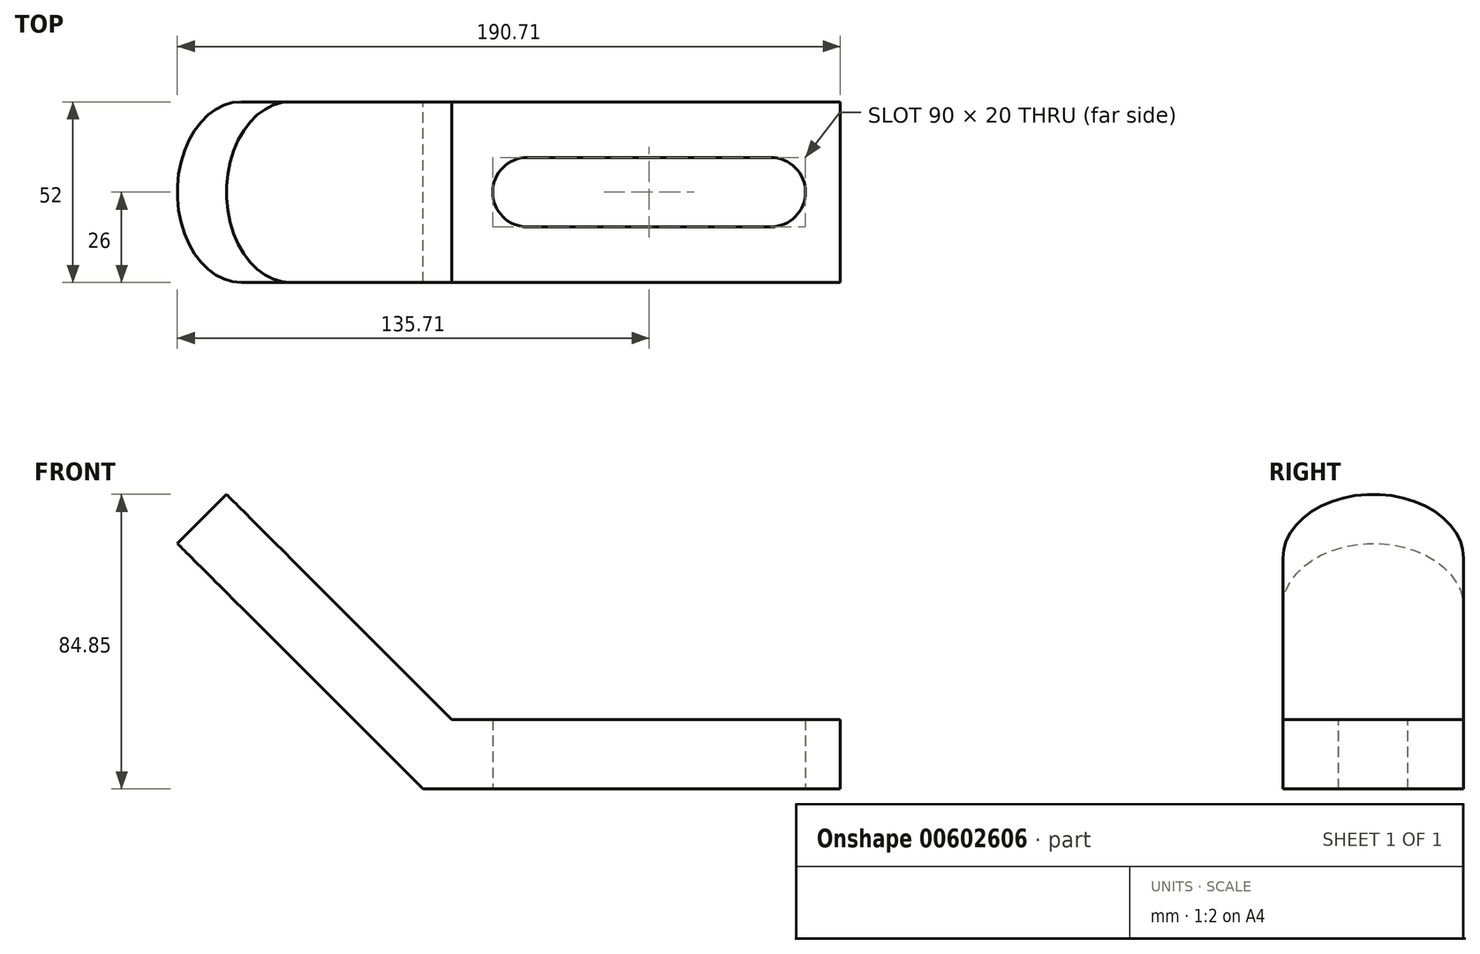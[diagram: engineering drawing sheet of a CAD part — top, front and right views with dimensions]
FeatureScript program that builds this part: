
annotation { "Feature Type Name" : "Feature", "Feature Type Description" : "" }
export const myFeature = defineFeature(function(context is Context, id is Id, definition is map)
    precondition{}
    {
        {
            var Q0;
            Q0=qCreatedBy(makeId("Front.planeOp"),FACE);
            var sketch = newSketch(context, id + "F0", { "sketchPlane" : qUnion([Q0])});
            skLineSegment(sketch, "E0.bottom", {"start": v(0, 0) * mm, "end": v(-120, 0) * mm});
            skLineSegment(sketch, "E0.left", {"start": v(0, 0) * mm, "end": v(0, 20) * mm});
            skLineSegment(sketch, "E1", {"start": v(-120, 0) * mm, "end": v(-190.71, 70.71) * mm});
            skLineSegment(sketch, "E2", {"start": v(-190.71, 70.71) * mm, "end": v(-176.57, 84.85) * mm});
            skLineSegment(sketch, "E3", {"start": v(-176.57, 84.85) * mm, "end": v(-111.72, 20) * mm});
            skLineSegment(sketch, "E4", {"start": v(0, 20) * mm, "end": v(-111.72, 20) * mm});
            skSolve(sketch);
        }
        {
            var Q0;
            Q0=makeQuery(id+"F0.imprint","IMPRINT",FACE,{"disambiguationData":[TD([[makeQuery(id+"F0.imprint","IMPRINT",EDGE,{"derivedFrom":sQuery(id+"F0.wireOp",EDGE,"E0.bottom")}),-1.0]])]});
            var Q1;
            Q1=makeQuery(id+"F0.imprint","IMPRINT",FACE,{"disambiguationData":[TD([[makeQuery(id+"F0.imprint","IMPRINT",EDGE,{"derivedFrom":sQuery(id+"F0.wireOp",EDGE,"n1ADsmMW-Lfod-etTo-9KBK-WFseRF6eV8BT")}),1.0]])]});
            extrude(context, id + "F1", {"entities" : qUnion([Q0, Q1]), "depth" : 52 * mm, "offsetDistance" : 25 * mm});
        }
        {
            var Q0;
            Q0=makeQuery(id+"F1.opExtrude","SWEPT_FACE",FACE,{"disambiguationData":[OSD([sQuery(id+"F0.wireOp",EDGE,"E3")])]});
            var sketch = newSketch(context, id + "F2", { "sketchPlane" : qUnion([Q0])});
            skCircle(sketch, "E5", {"center": v(-158.85, -26) * mm, "radius": 10 * mm});
            skSolve(sketch);
        }
        {
            var Q0;
            Q0=makeQuery(id+"F2.imprint","IMPRINT",FACE,{"disambiguationData":[TD([[makeQuery(id+"F2.imprint","IMPRINT",EDGE,{"derivedFrom":sQuery(id+"F2.wireOp",EDGE,"E5")}),1.0]])]});
            extrude(context, id + "F3", {"entities" : qUnion([Q0]), "operationType" : NewBodyOperationType.REMOVE, "oppositeDirection" : true, "depth" : 25 * mm, "offsetDistance" : 25 * mm});
        }
        {
            var Q0;
            Q0=makeQuery(id+"F1.opExtrude","CAP_EDGE",EDGE,{"disambiguationData":[OSD([sQuery(id+"F0.wireOp",EDGE,"E2")])],"isStart":true});
            var Q1;
            Q1=makeQuery(id+"F1.opExtrude","CAP_EDGE",EDGE,{"disambiguationData":[OSD([sQuery(id+"F0.wireOp",EDGE,"E2")])],"isStart":false});
            fillet(context, id + "F4", {"entities" : qUnion([Q0, Q1]), "radius" : 26 * mm, "tangentPropagation" : true, "allowEdgeOverflow" : false});
        }
        {
            var Q0;
            Q0=makeQuery(id+"F1.opExtrude","SWEPT_FACE",FACE,{"disambiguationData":[OSD([sQuery(id+"F0.wireOp",EDGE,"E4")])]});
            var sketch = newSketch(context, id + "F5", { "sketchPlane" : qUnion([Q0])});
            skLineSegment(sketch, "E6", {"start": v(0, 0) * mm, "end": v(0, -52) * mm});
            skLineSegment(sketch, "E7.top", {"start": v(-100, -16) * mm, "end": v(-10, -16) * mm});
            skLineSegment(sketch, "E7.left", {"start": v(-100, -26) * mm, "end": v(-100, -16) * mm});
            skLineSegment(sketch, "E7.right", {"start": v(-10, -26) * mm, "end": v(-10, -16) * mm});
            skLineSegment(sketch, "E8.top", {"start": v(-100, -36) * mm, "end": v(-10, -36) * mm});
            skLineSegment(sketch, "E8.left", {"start": v(-100, -26) * mm, "end": v(-100, -36) * mm});
            skLineSegment(sketch, "E8.right", {"start": v(-10, -26) * mm, "end": v(-10, -36) * mm});
            skSolve(sketch);
        }
        {
            var Q0;
            Q0=makeQuery(id+"F5.imprint","IMPRINT",FACE,{"disambiguationData":[TD([[makeQuery(id+"F5.imprint","IMPRINT",EDGE,{"derivedFrom":sQuery(id+"F5.wireOp",EDGE,"E7.top")}),-1.0]])]});
            extrude(context, id + "F6", {"entities" : qUnion([Q0]), "operationType" : NewBodyOperationType.REMOVE, "oppositeDirection" : true, "depth" : 25 * mm, "offsetDistance" : 25 * mm});
        }
        {
            var Q0;
            Q0=makeQuery(id+"F6.boolean.opBoolean","COPY",EDGE,{"derivedFrom":makeQuery(id+"F6.opExtrude","SWEPT_EDGE",EDGE,{"disambiguationData":[OSD([sQuery(id+"F5.wireOp",EDGE,"E7.top"),sQuery(id+"F5.wireOp",EDGE,"E7.right")])]})});
            var Q1;
            Q1=makeQuery(id+"F6.boolean.opBoolean","COPY",EDGE,{"derivedFrom":makeQuery(id+"F6.opExtrude","SWEPT_EDGE",EDGE,{"disambiguationData":[OSD([sQuery(id+"F5.wireOp",EDGE,"E8.top"),sQuery(id+"F5.wireOp",EDGE,"E8.right")])]})});
            var Q2;
            Q2=makeQuery(id+"F6.boolean.opBoolean","COPY",EDGE,{"derivedFrom":makeQuery(id+"F6.opExtrude","SWEPT_EDGE",EDGE,{"disambiguationData":[OSD([sQuery(id+"F5.wireOp",EDGE,"E7.top"),sQuery(id+"F5.wireOp",EDGE,"E7.left")])]})});
            var Q3;
            Q3=makeQuery(id+"F6.boolean.opBoolean","COPY",EDGE,{"derivedFrom":makeQuery(id+"F6.opExtrude","SWEPT_EDGE",EDGE,{"disambiguationData":[OSD([sQuery(id+"F5.wireOp",EDGE,"E8.top"),sQuery(id+"F5.wireOp",EDGE,"E8.left")])]})});
            fillet(context, id + "F7", {"entities" : qUnion([Q0, Q1, Q2, Q3]), "radius" : 10 * mm, "tangentPropagation" : true, "allowEdgeOverflow" : false});
        }
    });
